# Revit family: QF_Cool-Compact_Abfallkuehler_3x240L_EK
name_source: partatom
category: Sonderausstattung
units: mm (PartAtom-declared; Revit-internal decimal feet)

## family parameters
Arbeitsebenenbasiert = Nein
Beim Laden mit Abzugskörper schneiden = Nein
Bemaßung runder Anschluss = Durchmesser verwenden
Gemeinsam genutzt = Nein
Immer vertikal = Ja
OmniClass-Nummer = 23.70.30.21.11
OmniClass-Titel = Complete Solid Waste Removal Systems
Raumberechnungspunkt = Nein
Teiletyp = Normal

## types (1)
- 1NAC / 230 V / 50 Hz
    Anzahl der Pole = 1
    Beschreibung = Konfiskatkühler (3 x 240 Liter), eigengekühlt/steckerfertig
    CE Kennzeichnung = Ja
    Datenschnittstelle = Ja
    Datenschnittstelle Beschreibung = RS 485
    Frequenz = 50 Hz
    Gewicht = 255.00 kg
    Hersteller = Cool Compact
    Höhe = 1170 mm  [stored 3.83858 ft]
    Kälte Klimaklasse = 5
    Kälte Tauwasserablauf = Nein
    Kälte Verdampfungstemperatur = -15 °C
    Kälteleistung = 322 W
    Kältemittel = R290
    Kältemittelmenge = 95
    Länge Gerätebreite = 2400 mm  [stored 7.87402 ft]
    Modell = AKM032400
    Phasen = 1
    Schalldruckpegel = 59 dB
    Spannung = 230 V
    Stecker System = Schuko / T13
    Tiefe = 870 mm  [stored 2.85433 ft]
    URL = https://www.coolcompact.de
    Vorgabe-Ansicht = 0 mm  [stored 0 ft]
    Watt Leistung = 400 W
    Zuleitung zum Gerät im Lieferumfang = Ja

note: [stored X ft] marks values corroborated as IEEE doubles in the binary element streams (Revit-internal decimal feet)
